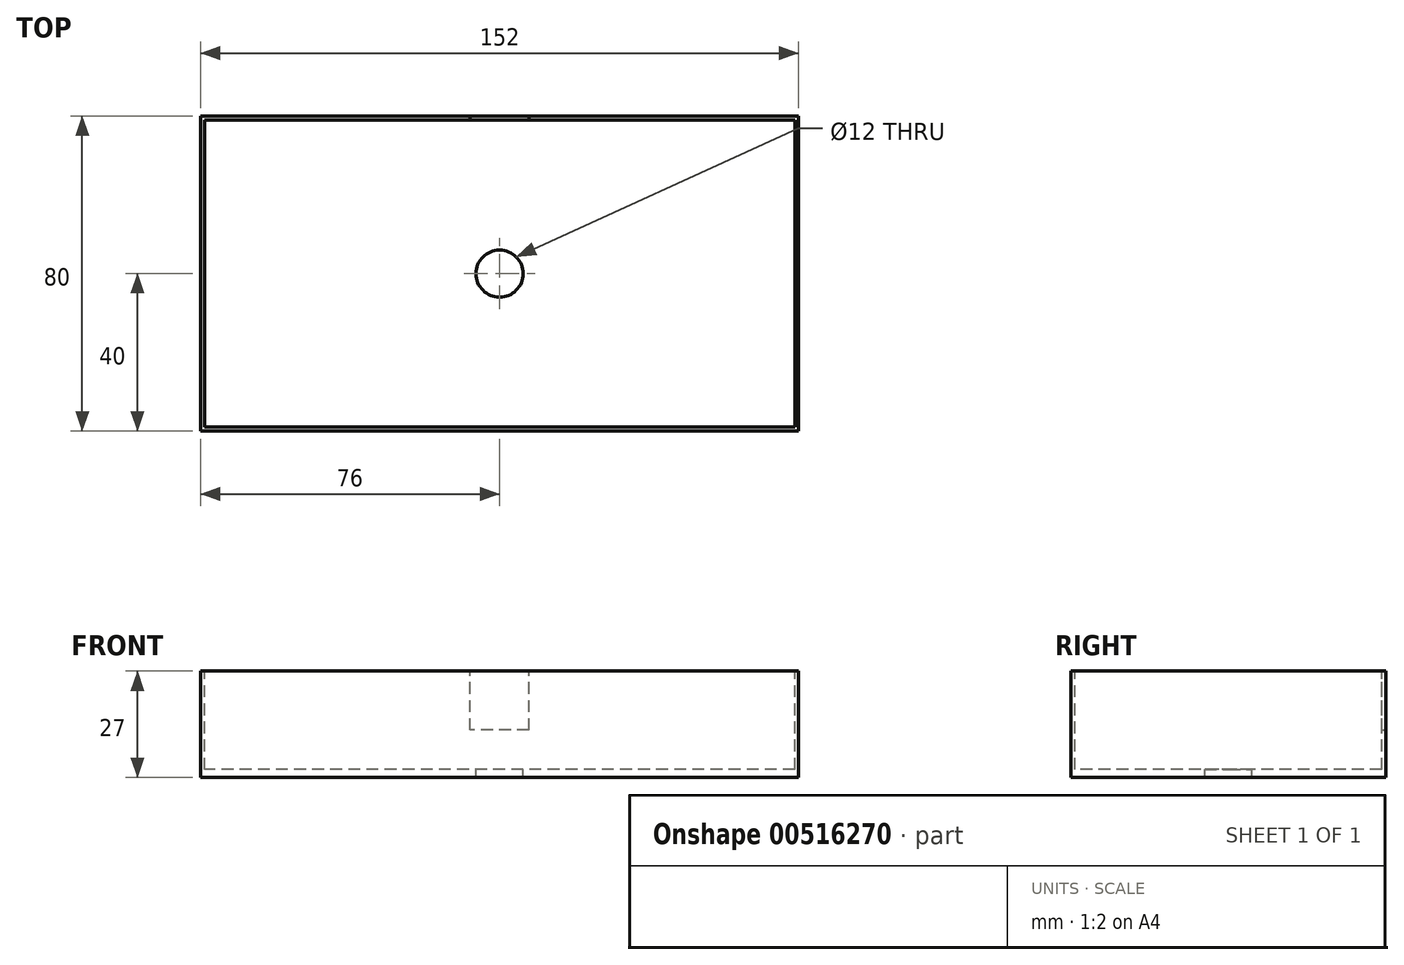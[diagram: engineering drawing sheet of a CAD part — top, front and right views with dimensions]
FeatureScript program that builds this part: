
annotation { "Feature Type Name" : "Feature", "Feature Type Description" : "" }
export const myFeature = defineFeature(function(context is Context, id is Id, definition is map)
    precondition{}
    {
        {
            var Q0;
            Q0=qCreatedBy(makeId("Top.planeOp"),FACE);
            var sketch = newSketch(context, id + "F0", { "sketchPlane" : qUnion([Q0])});
            skLineSegment(sketch, "E0.bottom", {"start": v(76, 40) * mm, "end": v(-76, 40) * mm});
            skLineSegment(sketch, "E0.top", {"start": v(76, -40) * mm, "end": v(-76, -40) * mm});
            skLineSegment(sketch, "E0.left", {"start": v(76, 40) * mm, "end": v(76, -40) * mm});
            skLineSegment(sketch, "E0.right", {"start": v(-76, 40) * mm, "end": v(-76, -40) * mm});
            skPoint(sketch, "E0.middle", {"position": v(0, 0) * mm});
            skSolve(sketch);
        }
        {
            var Q0;
            Q0=makeQuery(id+"F0.imprint","IMPRINT",FACE,{"disambiguationData":[TD([[makeQuery(id+"F0.imprint","IMPRINT",EDGE,{"derivedFrom":sQuery(id+"F0.wireOp",EDGE,"E0.bottom")}),1.0]])]});
            extrude(context, id + "F1", {"entities" : qUnion([Q0]), "depth" : 27 * mm});
        }
        {
            var Q0;
            Q0=makeQuery(id+"F1.opExtrude","CAP_FACE",FACE,{"disambiguationData":[OSD([sQuery(id+"F0.wireOp",EDGE,"E0.bottom"),sQuery(id+"F0.wireOp",EDGE,"E0.top"),sQuery(id+"F0.wireOp",EDGE,"E0.left"),sQuery(id+"F0.wireOp",EDGE,"E0.right")])],"isStart":false});
            var sketch = newSketch(context, id + "F2", { "sketchPlane" : qUnion([Q0])});
            skLineSegment(sketch, "E1.bottom", {"start": v(75, 39) * mm, "end": v(-75, 39) * mm});
            skLineSegment(sketch, "E1.top", {"start": v(75, -39) * mm, "end": v(-75, -39) * mm});
            skLineSegment(sketch, "E1.left", {"start": v(75, 39) * mm, "end": v(75, -39) * mm});
            skLineSegment(sketch, "E1.right", {"start": v(-75, 39) * mm, "end": v(-75, -39) * mm});
            skPoint(sketch, "E1.middle", {"position": v(0, 0) * mm});
            skSolve(sketch);
        }
        {
            var Q0;
            Q0=makeQuery(id+"F2.imprint","IMPRINT",FACE,{"disambiguationData":[TD([[makeQuery(id+"F2.imprint","IMPRINT",EDGE,{"derivedFrom":sQuery(id+"F2.wireOp",EDGE,"E1.bottom")}),1.0]])]});
            extrude(context, id + "F3", {"entities" : qUnion([Q0]), "operationType" : NewBodyOperationType.REMOVE, "oppositeDirection" : true, "depth" : 25 * mm});
        }
        {
            var Q0;
            Q0=makeQuery(id+"F3.boolean.opBoolean","COPY",FACE,{"derivedFrom":makeQuery(id+"F3.opExtrude","CAP_FACE",FACE,{"disambiguationData":[OSD([sQuery(id+"F2.wireOp",EDGE,"E1.bottom"),sQuery(id+"F2.wireOp",EDGE,"E1.top"),sQuery(id+"F2.wireOp",EDGE,"E1.left"),sQuery(id+"F2.wireOp",EDGE,"E1.right")])],"isStart":false})});
            var sketch = newSketch(context, id + "F4", { "sketchPlane" : qUnion([Q0])});
            skCircle(sketch, "E2", {"center": v(0, 0) * mm, "radius": 6 * mm});
            skSolve(sketch);
        }
        {
            var Q0;
            Q0=makeQuery(id+"F4.imprint","IMPRINT",FACE,{"disambiguationData":[TD([[makeQuery(id+"F4.imprint","IMPRINT",EDGE,{"derivedFrom":sQuery(id+"F4.wireOp",EDGE,"E2")}),1.0]])]});
            extrude(context, id + "F5", {"entities" : qUnion([Q0]), "operationType" : NewBodyOperationType.REMOVE, "oppositeDirection" : true, "depth" : 5 * mm});
        }
        {
            var Q0;
            Q0=makeQuery(id+"F1.opExtrude","SWEPT_FACE",FACE,{"disambiguationData":[OSD([sQuery(id+"F0.wireOp",EDGE,"E0.bottom")])]});
            var sketch = newSketch(context, id + "F6", { "sketchPlane" : qUnion([Q0])});
            skLineSegment(sketch, "E3.bottom", {"start": v(-7.5, 12) * mm, "end": v(7.5, 12) * mm});
            skLineSegment(sketch, "E3.top", {"start": v(-7.5, 42) * mm, "end": v(7.5, 42) * mm});
            skLineSegment(sketch, "E3.left", {"start": v(-7.5, 12) * mm, "end": v(-7.5, 42) * mm});
            skLineSegment(sketch, "E3.right", {"start": v(7.5, 12) * mm, "end": v(7.5, 42) * mm});
            skPoint(sketch, "E3.middle", {"position": v(0, 27) * mm});
            skSolve(sketch);
        }
        {
            var Q0;
            {var subQ0=sQuery(id+"F6.wireOp",EDGE,"E3.bottom");Q0=makeQuery(id+"F6.imprint","IMPRINT",FACE,{"disambiguationData":[TD([[makeQuery(id+"F6.imprint","IMPRINT",EDGE,{"derivedFrom":subQ0}),1.0]])]});}
            extrude(context, id + "F7", {"entities" : qUnion([Q0]), "operationType" : NewBodyOperationType.REMOVE, "oppositeDirection" : true, "depth" : 1 * mm});
        }
    });
